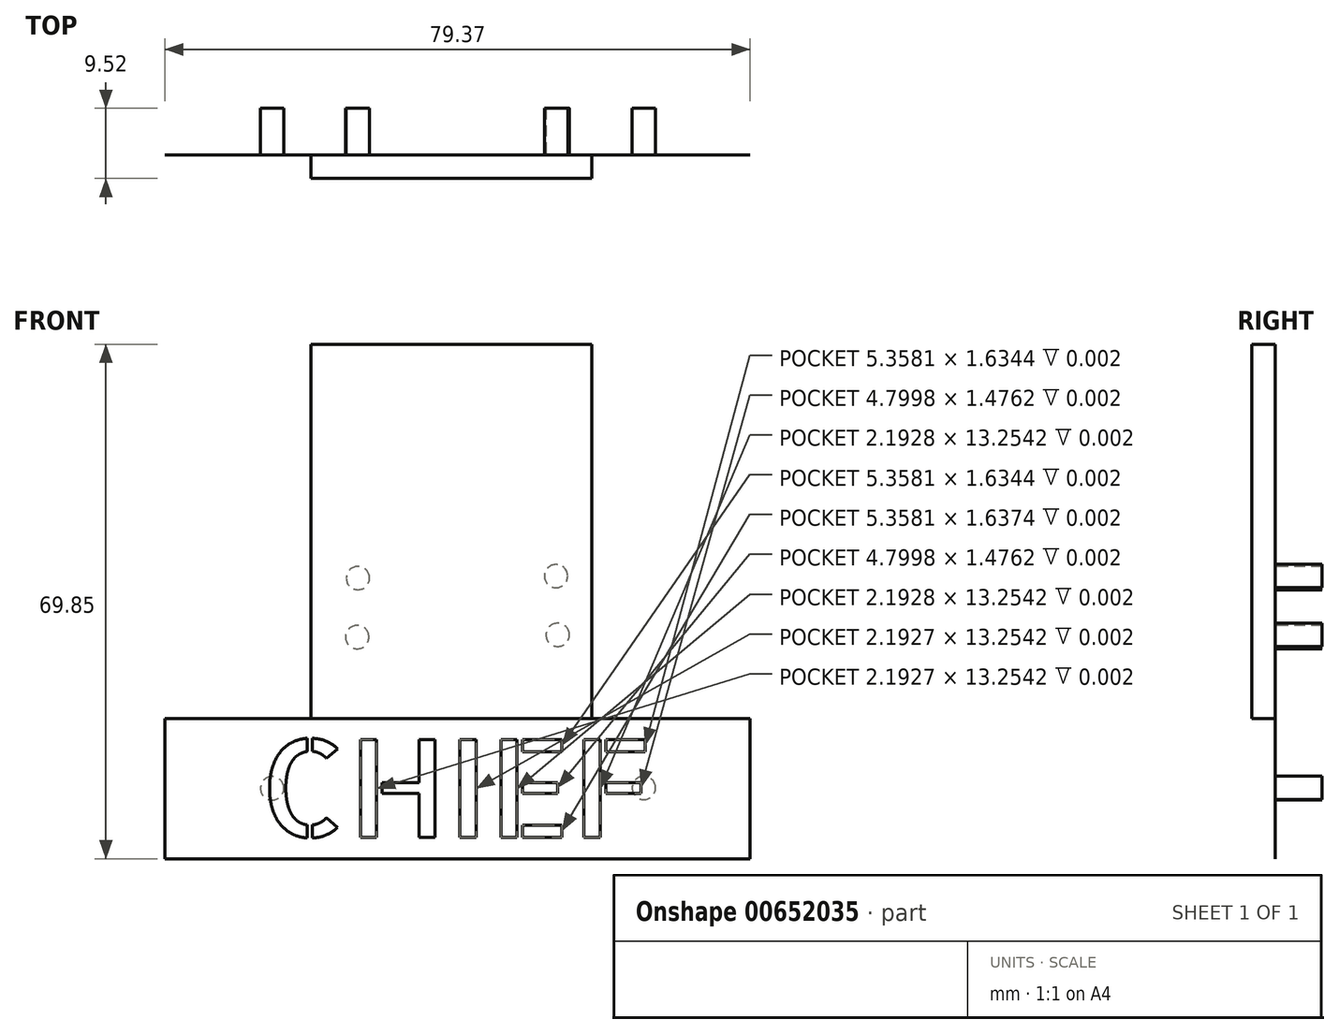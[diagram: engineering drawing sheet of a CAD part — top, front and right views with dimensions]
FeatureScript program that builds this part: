
annotation { "Feature Type Name" : "Feature", "Feature Type Description" : "" }
export const myFeature = defineFeature(function(context is Context, id is Id, definition is map)
    precondition{}
    {
        {
            var Q0;
            Q0=qCreatedBy(makeId("Front.planeOp"),FACE);
            var sketch = newSketch(context, id + "F0", { "sketchPlane" : qUnion([Q0])});
            skLineSegment(sketch, "E0", {"start": v(-92.65, -45.27) * mm, "end": v(-41.85, -45.27) * mm, "construction": true});
            skLineSegment(sketch, "E1.bottom", {"start": v(-80.75, -16.7) * mm, "end": v(-53.76, -16.7) * mm, "construction": true});
            skLineSegment(sketch, "E1.top", {"start": v(-80.75, -24.64) * mm, "end": v(-53.76, -24.64) * mm, "construction": true});
            skLineSegment(sketch, "E1.left", {"start": v(-80.75, -16.7) * mm, "end": v(-80.75, -24.64) * mm, "construction": true});
            skLineSegment(sketch, "E1.right", {"start": v(-53.76, -16.7) * mm, "end": v(-53.76, -24.64) * mm, "construction": true});
            skLineSegment(sketch, "E2", {"start": v(-67.25, -45.27) * mm, "end": v(-67.25, -16.7) * mm, "construction": true});
            skLineSegment(sketch, "E3.bottom", {"start": v(-106.94, -35.75) * mm, "end": v(-27.57, -35.75) * mm});
            skLineSegment(sketch, "E3.top", {"start": v(-106.94, -54.8) * mm, "end": v(-27.57, -54.8) * mm});
            skLineSegment(sketch, "E3.left", {"start": v(-106.94, -35.75) * mm, "end": v(-106.94, -54.8) * mm});
            skLineSegment(sketch, "E3.right", {"start": v(-27.57, -35.75) * mm, "end": v(-27.57, -54.8) * mm});
            skLineSegment(sketch, "E4.top", {"start": v(-109.09, -35.75) * mm, "end": v(-27.57, -35.75) * mm, "construction": true});
            skLineSegment(sketch, "E5.top", {"start": v(-87.25, -35.75) * mm, "end": v(-47.25, -35.75) * mm});
            skLineSegment(sketch, "E6.bottom", {"start": v(-93.45, -35.75) * mm, "end": v(-41.06, -35.75) * mm});
            skLineSegment(sketch, "E7.bottom", {"start": v(-87.15, 15.05) * mm, "end": v(-49.05, 15.05) * mm});
            skLineSegment(sketch, "E7.top", {"start": v(-87.15, -35.75) * mm, "end": v(-49.05, -35.75) * mm});
            skLineSegment(sketch, "E7.left", {"start": v(-87.15, 15.05) * mm, "end": v(-87.15, -35.75) * mm});
            skLineSegment(sketch, "E7.right", {"start": v(-49.05, 15.05) * mm, "end": v(-49.05, -35.75) * mm});
            skCircle(sketch, "E8", {"center": v(-80.75, -16.7) * mm, "radius": 1.59 * mm});
            skCircle(sketch, "E9", {"center": v(-53.87, -16.44) * mm, "radius": 1.59 * mm});
            skCircle(sketch, "E10", {"center": v(-53.65, -24.4) * mm, "radius": 1.59 * mm});
            skCircle(sketch, "E11", {"center": v(-80.84, -24.7) * mm, "radius": 1.59 * mm});
            skCircle(sketch, "E12", {"center": v(-41.96, -45.2) * mm, "radius": 1.59 * mm});
            skCircle(sketch, "E13", {"center": v(-92.4, -45.24) * mm, "radius": 1.59 * mm});
            skSolve(sketch);
        }
        {
            var Q0;
            Q0=makeQuery(id+"F0.imprint","IMPRINT",FACE,{"disambiguationData":[TD([[makeQuery(id+"F0.imprint","IMPRINT",EDGE,{"derivedFrom":sQuery(id+"F0.wireOp",EDGE,"E3.top")}),1.0]])]});
            var Q1;
            Q1=makeQuery(id+"F0.imprint","IMPRINT",FACE,{"disambiguationData":[TD([[makeQuery(id+"F0.imprint","IMPRINT",EDGE,{"derivedFrom":sQuery(id+"F0.wireOp",EDGE,"E13")}),1.0]])]});
            var Q2;
            Q2=makeQuery(id+"F0.imprint","IMPRINT",FACE,{"disambiguationData":[TD([[makeQuery(id+"F0.imprint","IMPRINT",EDGE,{"derivedFrom":sQuery(id+"F0.wireOp",EDGE,"E12")}),1.0]])]});
            extrude(context, id + "F1", {"entities" : qUnion([Q0, Q1, Q2]), "depth" : 1 / 203.2 * mm, "offsetDistance" : 25 * mm});
        }
        {
            var Q0;
            Q0=makeQuery(id+"F1.opExtrude","CAP_FACE",FACE,{"disambiguationData":[OSD([sQuery(id+"F0.wireOp",EDGE,"E3.bottom"),sQuery(id+"F0.wireOp",EDGE,"E3.top"),sQuery(id+"F0.wireOp",EDGE,"E3.left"),sQuery(id+"F0.wireOp",EDGE,"E3.right")])],"isStart":false});
            var sketch = newSketch(context, id + "F2", { "sketchPlane" : qUnion([Q0])});
            skText(sketch, "E14", { "text": "CHIEF", "fontName": "AllertaStencil-Regular.ttf"});
            skLineSegment(sketch, "E15", {"start": v(-82.05, -38.65) * mm, "end": v(-82.05, -35.75) * mm, "construction": true});
            skLineSegment(sketch, "E16", {"start": v(-82.35, -51.9) * mm, "end": v(-82.35, -54.8) * mm, "construction": true});
            skLineSegment(sketch, "E17", {"start": v(-94.05, -45.91) * mm, "end": v(-106.94, -45.91) * mm, "construction": true});
            skLineSegment(sketch, "E18", {"start": v(-40.46, -45.91) * mm, "end": v(-27.57, -45.91) * mm, "construction": true});
            const initialGuessF2  = {"E14": [-0.09416, -0.0519, 1, 0, 0.01326]};
            skSetInitialGuess(sketch, initialGuessF2);
            skSolve(sketch);
        }
        {
            var Q0;
            Q0=qSketchRegion(id+"F2",true);
            extrude(context, id + "F3", {"entities" : qUnion([Q0]), "operationType" : NewBodyOperationType.REMOVE, "oppositeDirection" : true, "depth" : 1 / 406.4 * mm, "offsetDistance" : 25 * mm});
        }
        {
            var Q0;
            Q0=makeQuery(id+"F0.imprint","IMPRINT",FACE,{"disambiguationData":[TD([[makeQuery(id+"F0.imprint","IMPRINT",EDGE,{"derivedFrom":sQuery(id+"F0.wireOp",EDGE,"E7.bottom")}),-1.0]])]});
            var Q1;
            Q1=makeQuery(id+"F0.imprint","IMPRINT",FACE,{"disambiguationData":[TD([[makeQuery(id+"F0.imprint","IMPRINT",EDGE,{"derivedFrom":sQuery(id+"F0.wireOp",EDGE,"E8")}),1.0]])]});
            var Q2;
            Q2=makeQuery(id+"F0.imprint","IMPRINT",FACE,{"disambiguationData":[TD([[makeQuery(id+"F0.imprint","IMPRINT",EDGE,{"derivedFrom":sQuery(id+"F0.wireOp",EDGE,"E11")}),1.0]])]});
            var Q3;
            Q3=makeQuery(id+"F0.imprint","IMPRINT",FACE,{"disambiguationData":[TD([[makeQuery(id+"F0.imprint","IMPRINT",EDGE,{"derivedFrom":sQuery(id+"F0.wireOp",EDGE,"E9")}),1.0]])]});
            var Q4;
            Q4=makeQuery(id+"F0.imprint","IMPRINT",FACE,{"disambiguationData":[TD([[makeQuery(id+"F0.imprint","IMPRINT",EDGE,{"derivedFrom":sQuery(id+"F0.wireOp",EDGE,"E10")}),1.0]])]});
            extrude(context, id + "F4", {"entities" : qUnion([Q0, Q1, Q2, Q3, Q4]), "operationType" : NewBodyOperationType.ADD, "depth" : 3.17 * mm, "offsetDistance" : 25.4 * mm});
        }
        {
            var Q0;
            Q0=makeQuery(id+"F0.imprint","IMPRINT",FACE,{"disambiguationData":[TD([[makeQuery(id+"F0.imprint","IMPRINT",EDGE,{"derivedFrom":sQuery(id+"F0.wireOp",EDGE,"E9")}),1.0]])]});
            var Q1;
            Q1=makeQuery(id+"F0.imprint","IMPRINT",FACE,{"disambiguationData":[TD([[makeQuery(id+"F0.imprint","IMPRINT",EDGE,{"derivedFrom":sQuery(id+"F0.wireOp",EDGE,"E8")}),1.0]])]});
            var Q2;
            Q2=makeQuery(id+"F0.imprint","IMPRINT",FACE,{"disambiguationData":[TD([[makeQuery(id+"F0.imprint","IMPRINT",EDGE,{"derivedFrom":sQuery(id+"F0.wireOp",EDGE,"E11")}),1.0]])]});
            var Q3;
            Q3=makeQuery(id+"F0.imprint","IMPRINT",FACE,{"disambiguationData":[TD([[makeQuery(id+"F0.imprint","IMPRINT",EDGE,{"derivedFrom":sQuery(id+"F0.wireOp",EDGE,"E10")}),1.0]])]});
            extrude(context, id + "F5", {"entities" : qUnion([Q0, Q1, Q2, Q3]), "operationType" : NewBodyOperationType.ADD, "oppositeDirection" : true, "depth" : 6.35 * mm, "offsetDistance" : 25.4 * mm});
        }
        {
            var Q0;
            Q0=makeQuery(id+"F0.imprint","IMPRINT",FACE,{"disambiguationData":[TD([[makeQuery(id+"F0.imprint","IMPRINT",EDGE,{"derivedFrom":sQuery(id+"F0.wireOp",EDGE,"E12")}),1.0]])]});
            var Q1;
            Q1=makeQuery(id+"F0.imprint","IMPRINT",FACE,{"disambiguationData":[TD([[makeQuery(id+"F0.imprint","IMPRINT",EDGE,{"derivedFrom":sQuery(id+"F0.wireOp",EDGE,"E13")}),1.0]])]});
            var Q2;
            Q2=sQuery(id+"F0.wireOp",EDGE,"E13");
            var Q3;
            Q3=sQuery(id+"F0.wireOp",EDGE,"E12");
            extrude(context, id + "F6", {"entities" : qUnion([Q0, Q1]), "operationType" : NewBodyOperationType.ADD, "surfaceOperationType" : NewSurfaceOperationType.ADD, "surfaceEntities" : qUnion([Q2, Q3]), "oppositeDirection" : true, "depth" : 6.35 * mm, "offsetDistance" : 25.4 * mm});
        }
    });
